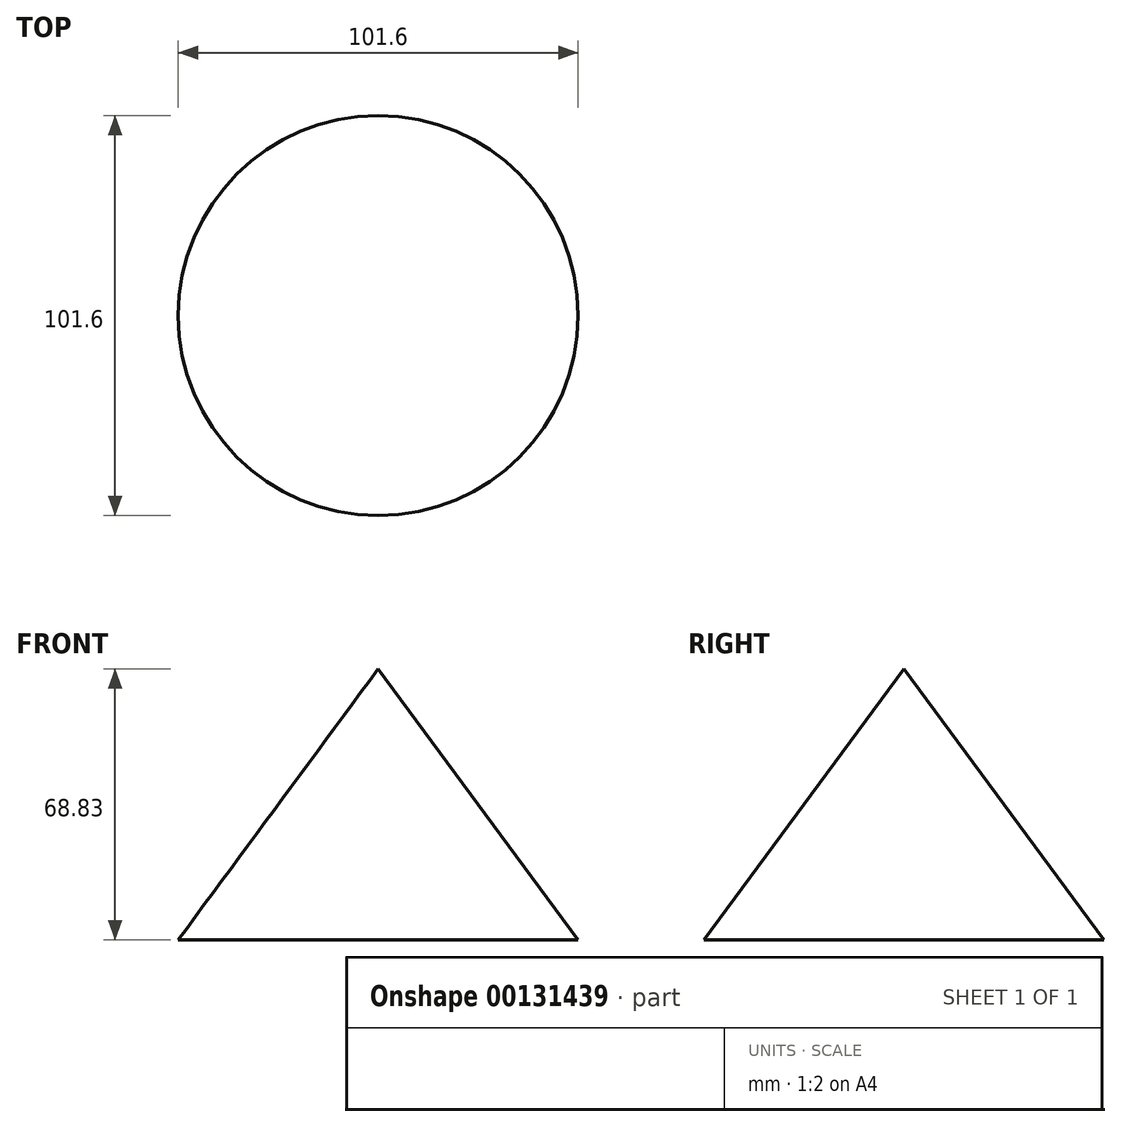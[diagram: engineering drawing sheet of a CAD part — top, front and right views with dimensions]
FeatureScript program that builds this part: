
annotation { "Feature Type Name" : "Feature", "Feature Type Description" : "" }
export const myFeature = defineFeature(function(context is Context, id is Id, definition is map)
    precondition{}
    {
        {
            var Q0;
            Q0=qCreatedBy(makeId("Front.planeOp"),FACE);
            var sketch = newSketch(context, id + "F0", { "sketchPlane" : qUnion([Q0])});
            skLineSegment(sketch, "E0", {"start": v(0, 68.83) * mm, "end": v(0, 0) * mm});
            skLineSegment(sketch, "E1", {"start": v(0, 0) * mm, "end": v(50.8, 0) * mm});
            skLineSegment(sketch, "E2", {"start": v(50.8, 0) * mm, "end": v(0, 68.83) * mm});
            skSolve(sketch);
        }
        {
            var Q0;
            Q0 = qSketchRegion(id + "F0", true);
            var Q1;
            Q1=sQuery(id+"F0.wireOp",EDGE,"E0");
            revolve(context, id + "F1", {"entities" : qUnion([Q0]), "axis" : qUnion([Q1]), "revolveType" : RevolveType.FULL});
        }
    });
